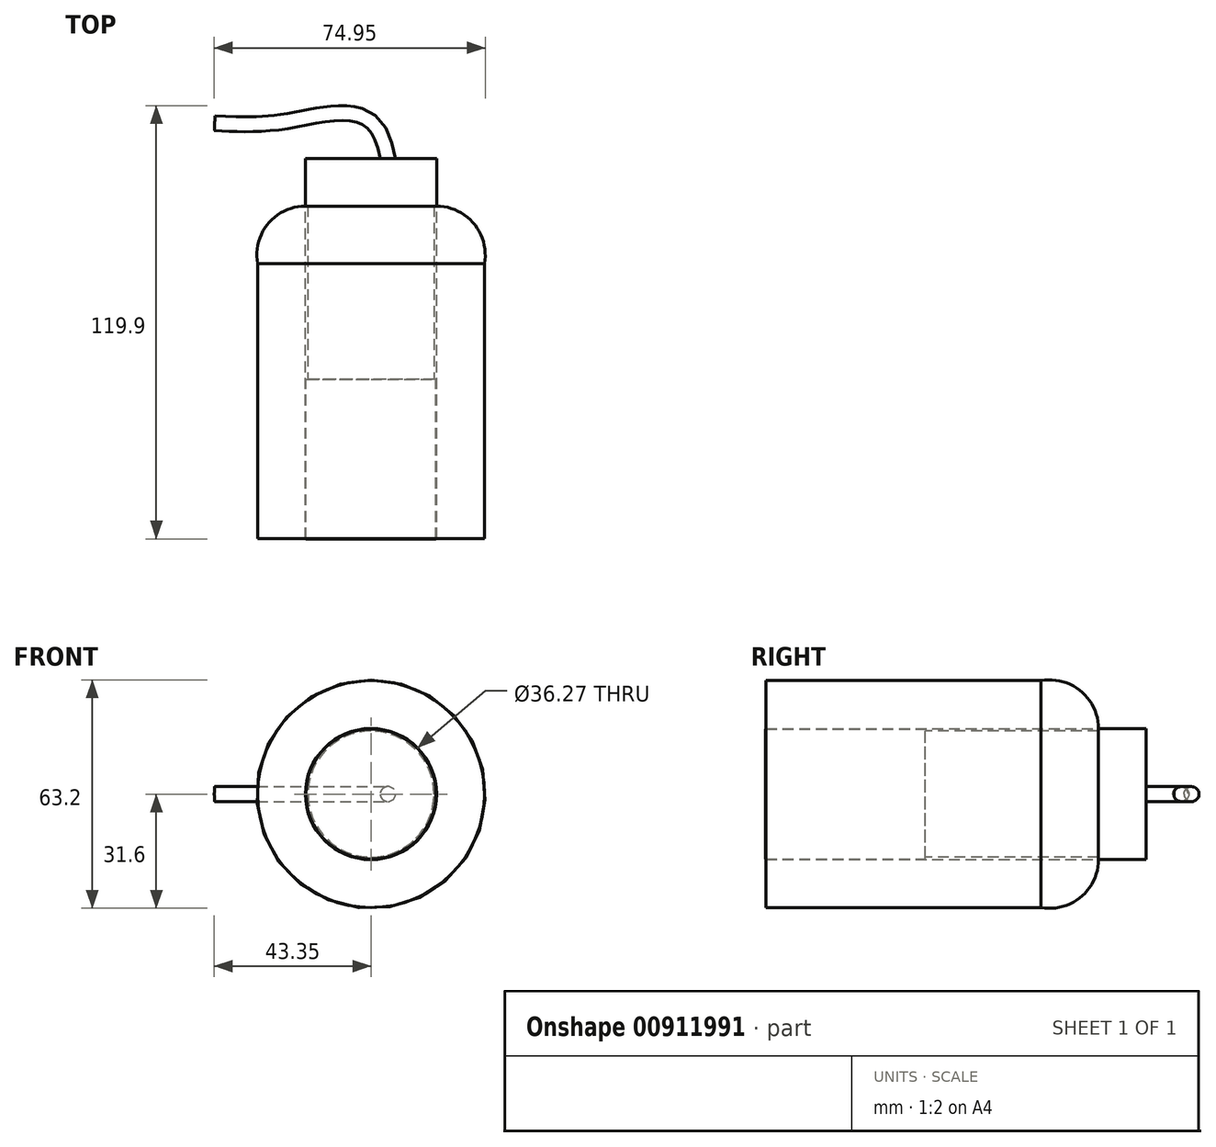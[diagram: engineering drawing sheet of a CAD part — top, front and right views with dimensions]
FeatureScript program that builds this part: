
annotation { "Feature Type Name" : "Feature", "Feature Type Description" : "" }
export const myFeature = defineFeature(function(context is Context, id is Id, definition is map)
    precondition{}
    {
        {
            var Q0;
            Q0=qCreatedBy(makeId("Top.planeOp"),FACE);
            var sketch = newSketch(context, id + "F0", { "sketchPlane" : qUnion([Q0])});
            skLineSegment(sketch, "E0", {"start": v(0, 34.8) * mm, "end": v(0, -45.23) * mm, "construction": true});
            skLineSegment(sketch, "E1", {"start": v(18.14, 34.41) * mm, "end": v(18.14, -44.08) * mm});
            skLineSegment(sketch, "E2", {"start": v(31.38, -44.08) * mm, "end": v(31.38, 32) * mm});
            skLineSegment(sketch, "E3", {"start": v(0, -45.23) * mm, "end": v(18.14, -44.08) * mm});
            skLineSegment(sketch, "E4", {"start": v(18.14, -44.08) * mm, "end": v(31.38, -44.08) * mm});
            skArc(sketch, "E5", {"start": v(31.38, 32) * mm, "mid": v(28.48, 43.03) * mm, "end": v(18.14, 47.87) * mm});
            skLineSegment(sketch, "E6", {"start": v(18.14, 47.87) * mm, "end": v(18.14, 34.41) * mm});
            skLineSegment(sketch, "E7", {"start": v(0, -39.91) * mm, "end": v(18.14, -39.91) * mm});
            skLineSegment(sketch, "E8", {"start": v(18.14, 47.87) * mm, "end": v(18.14, 61.02) * mm});
            skLineSegment(sketch, "E9", {"start": v(18.14, 61.02) * mm, "end": v(0, 61.02) * mm});
            skLineSegment(sketch, "E10", {"start": v(0, 61.02) * mm, "end": v(0, 47.87) * mm});
            skLineSegment(sketch, "E11", {"start": v(0, 47.87) * mm, "end": v(18.14, 47.87) * mm});
            skSolve(sketch);
        }
        {
            var Q0;
            Q0 = qSketchRegion(id + "F0", true);
            var Q1;
            Q1=makeQuery(id+"F0.imprint","IMPRINT",FACE,{"disambiguationData":[TD([[makeQuery(id+"F0.imprint","IMPRINT",EDGE,{"derivedFrom":sQuery(id+"F0.wireOp",EDGE,"E8")}),1.0]])]});
            var Q2;
            Q2=sQuery(id+"F0.wireOp",EDGE,"E0");
            revolve(context, id + "F1", {"surfaceOperationType" : NewSurfaceOperationType.NEW, "entities" : qUnion([Q0, Q1]), "axis" : qUnion([Q2]), "revolveType" : RevolveType.FULL});
        }
        {
            var Q0;
            Q0=qCreatedBy(makeId("Front.planeOp"),FACE);
            var sketch = newSketch(context, id + "F2", { "sketchPlane" : qUnion([Q0])});
            skCircle(sketch, "E12", {"center": v(0, 0) * mm, "radius": 17.99 * mm});
            skFitSpline(sketch, "E13", {"points": [v(0, 0) * mm, v(6.32, 2097.36) * mm, v(24.12, 2473.06) * mm, v(33.29, 2489.38) * mm, v(45.93, 2473.35) * mm], "startDerivative": vector(0.62, 3963.3) * mm, "endDerivative": vector(218.33, -382.53) * mm});
            skSolve(sketch);
        }
        {
            var Q0;
            Q0=makeQuery(id+"F2.imprint","IMPRINT",FACE,{"disambiguationData":[TD([[makeQuery(id+"F2.imprint","IMPRINT",EDGE,{"derivedFrom":sQuery(id+"F2.wireOp",EDGE,"E12")}),1.0]])]});
            extrude(context, id + "F3", {"entities" : qUnion([Q0]), "operationType" : NewBodyOperationType.ADD, "depth" : 44.2 * mm, "offsetDistance" : 25.4 * mm});
        }
        {
            var Q0;
            Q0=qCreatedBy(makeId("Top.planeOp"),FACE);
            var sketch = newSketch(context, id + "F4", { "sketchPlane" : qUnion([Q0])});
            skFitSpline(sketch, "E14", {"points": [v(0, 0) * mm, v(0, 71.06) * mm, v(-23, 71.25) * mm, v(-43.25, 70.62) * mm], "startDerivative": vector(28.88, 198.9) * mm, "endDerivative": vector(-74.5, 3.6) * mm});
            skSolve(sketch);
        }
        {
            var Q0;
            Q0=sQuery(id+"F4.wireOp",VERTEX,"E14.end");
            var Q1;
            Q1=sQuery(id+"F4.wireOp",EDGE,"E14");
            cPlane(context, id + "F5", {"entities" : qUnion([Q0, Q1]), "cplaneType" : CPlaneType.CURVE_POINT, "offset" : 25.4 * mm, "width" : 152.4 * mm, "height" : 152.4 * mm});
        }
        {
            var Q0;
            Q0=qCreatedBy(id+"F5.planeOp",FACE);
            var sketch = newSketch(context, id + "F6", { "sketchPlane" : qUnion([Q0])});
            skCircle(sketch, "E15", {"center": v(-68.62, 0) * mm, "radius": 2.06 * mm});
            skSolve(sketch);
        }
        {
            var Q0;
            Q0=makeQuery(id+"F6.imprint","IMPRINT",FACE,{"disambiguationData":[TD([[makeQuery(id+"F6.imprint","IMPRINT",EDGE,{"derivedFrom":sQuery(id+"F6.wireOp",EDGE,"E15")}),1.0]])]});
            var Q1;
            Q1=sQuery(id+"F4.wireOp",EDGE,"E14");
            sweep(context, id + "F7", {"operationType" : NewBodyOperationType.ADD, "profiles" : qUnion([Q0]), "path" : qUnion([Q1])});
        }
        {
            var Q0;
            Q0=makeQuery(id+"F3.opExtrude","CAP_FACE",FACE,{"disambiguationData":[OSD([sQuery(id+"F2.wireOp",EDGE,"E12")])],"isStart":true});
            var sketch = newSketch(context, id + "F8", { "sketchPlane" : qUnion([Q0])});
            skCircle(sketch, "E16", {"center": v(0, 0) * mm, "radius": 17.44 * mm});
            skSolve(sketch);
        }
        {
            var Q0;
            Q0 = qSketchRegion(id + "F8", true);
            extrude(context, id + "F9", {"entities" : qUnion([Q0]), "operationType" : NewBodyOperationType.ADD, "depth" : 48.26 * mm, "offsetDistance" : 25.4 * mm});
        }
    });
